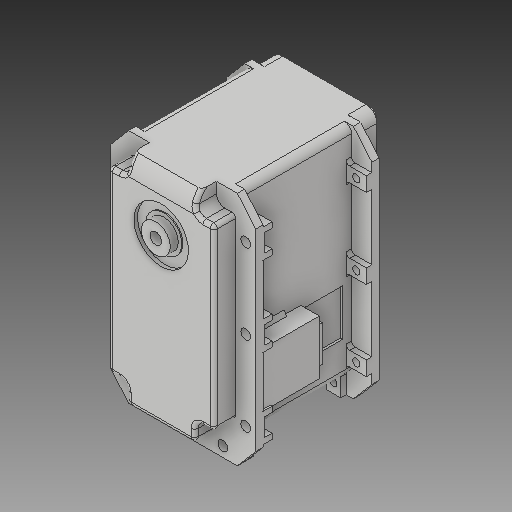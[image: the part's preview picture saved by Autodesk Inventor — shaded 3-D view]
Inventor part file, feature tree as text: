
AUTODESK INVENTOR PART (.ipt)
format: ipt  version: 2019 (Build 230136000, 136)  size: 539,136 bytes
history: native  units: in
note: dims shown in document units (in); Inventor stores cm internally (conversion verified against a paired STEP export)
features: other x3, sketch x1
ambient origin geometry x8: Origin, YZ Plane, XZ Plane, XY Plane, X Axis, Y Axis, Z Axis, Center Point
bodies: Solid1 (feature_tree)
feature tree (4):
  other  "MX-106T.ipt"
  other  "Solid1::MX-106T.ipt"
  other  "TaggingFeature1"
  sketch  "Sketch1"  dims[d0=0.3937in]
